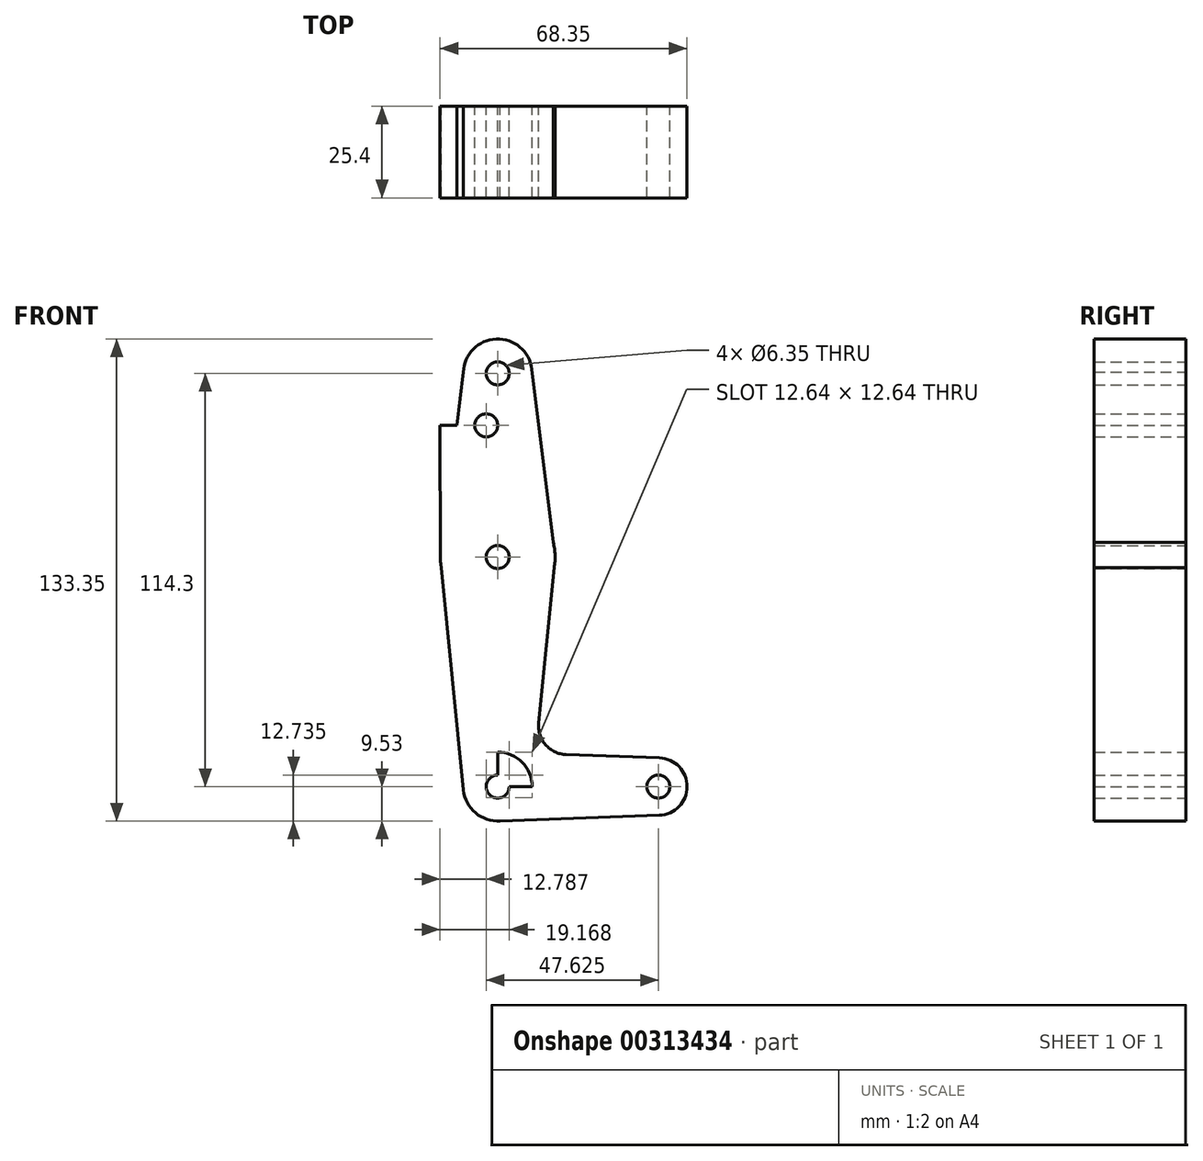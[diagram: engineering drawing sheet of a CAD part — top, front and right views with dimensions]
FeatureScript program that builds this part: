
annotation { "Feature Type Name" : "Feature", "Feature Type Description" : "" }
export const myFeature = defineFeature(function(context is Context, id is Id, definition is map)
    precondition{}
    {
        {
            var Q0;
            Q0=qCreatedBy(makeId("Front.planeOp"),FACE);
            var sketch = newSketch(context, id + "F0", { "sketchPlane" : qUnion([Q0])});
            skLineSegment(sketch, "E0", {"start": v(-42.5, 80.96) * mm, "end": v(-42.5, 30.16) * mm});
            skLineSegment(sketch, "E1", {"start": v(-42.5, 30.16) * mm, "end": v(-42.5, -33.34) * mm});
            skLineSegment(sketch, "E2", {"start": v(-42.5, -33.34) * mm, "end": v(1.95, -33.34) * mm});
            skCircle(sketch, "E3", {"center": v(-42.5, 80.96) * mm, "radius": 9.53 * mm});
            skCircle(sketch, "E4", {"center": v(-42.5, 30.16) * mm, "radius": 15.88 * mm});
            skCircle(sketch, "E5", {"center": v(-42.5, -33.34) * mm, "radius": 9.53 * mm});
            skCircle(sketch, "E6", {"center": v(1.95, -33.34) * mm, "radius": 7.94 * mm});
            skLineSegment(sketch, "E7", {"start": v(-52.02, 81.28) * mm, "end": v(-58.37, 29.97) * mm});
            skLineSegment(sketch, "E8", {"start": v(-58.37, 29.97) * mm, "end": v(-51.98, -34.28) * mm});
            skLineSegment(sketch, "E9", {"start": v(-31.18, -15.76) * mm, "end": v(-26.62, 29.97) * mm});
            skLineSegment(sketch, "E10", {"start": v(-26.62, 29.97) * mm, "end": v(-33.04, 82.12) * mm});
            skLineSegment(sketch, "E11", {"start": v(-23.55, -24.49) * mm, "end": v(2.23, -25.4) * mm});
            skLineSegment(sketch, "E12", {"start": v(-42.5, -42.87) * mm, "end": v(2.23, -41.27) * mm});
            skPoint(sketch, "E13.newPointA", {"position": v(-33.02, -34.28) * mm});
            skArc(sketch, "E13.filletArc", {"start": v(-31.18, -15.76) * mm, "mid": v(-29.25, -21.78) * mm, "end": v(-23.55, -24.49) * mm});
            skCircle(sketch, "E14", {"center": v(-42.5, 80.96) * mm, "radius": 3.18 * mm});
            skCircle(sketch, "E15", {"center": v(-42.5, 30.16) * mm, "radius": 3.18 * mm});
            skCircle(sketch, "E16", {"center": v(-42.5, -33.34) * mm, "radius": 3.18 * mm});
            skCircle(sketch, "E17", {"center": v(1.95, -33.34) * mm, "radius": 3.18 * mm});
            skCircle(sketch, "E18", {"center": v(-45.67, 66.58) * mm, "radius": 3.18 * mm});
            skLineSegment(sketch, "E19", {"start": v(-48.85, 66.58) * mm, "end": v(-58.46, 66.58) * mm});
            skLineSegment(sketch, "E20", {"start": v(-58.46, 66.58) * mm, "end": v(-58.37, 29.97) * mm});
            skLineSegment(sketch, "E21", {"start": v(-42.5, 30.16) * mm, "end": v(-58.37, 29.97) * mm});
            skSolve(sketch);
        }
        {
            var Q0;
            Q0 = qSketchRegion(id + "F0", true);
            extrude(context, id + "F1", {"entities" : qUnion([Q0]), "depth" : 25.4 * mm});
        }
    });
